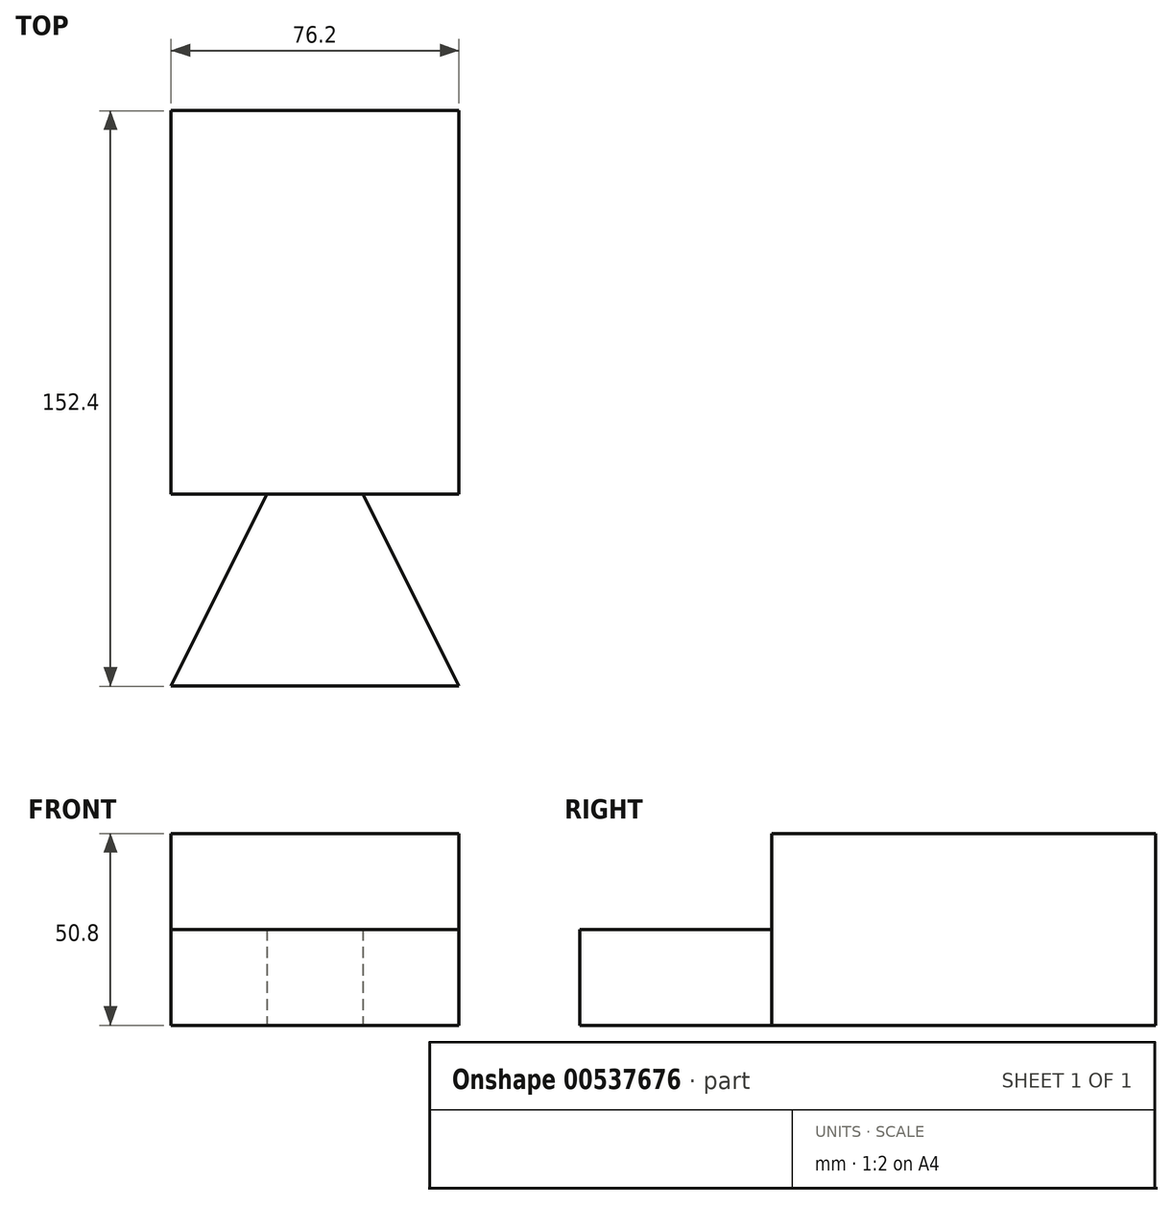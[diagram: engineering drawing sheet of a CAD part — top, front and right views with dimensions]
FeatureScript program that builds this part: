
annotation { "Feature Type Name" : "Feature", "Feature Type Description" : "" }
export const myFeature = defineFeature(function(context is Context, id is Id, definition is map)
    precondition{}
    {
        {
            var Q0;
            Q0=qCreatedBy(makeId("Top.planeOp"),FACE);
            var sketch = newSketch(context, id + "F0", { "sketchPlane" : qUnion([Q0])});
            skLineSegment(sketch, "E0.bottom", {"start": v(-123.66, 76.55) * mm, "end": v(-47.46, 76.55) * mm});
            skLineSegment(sketch, "E0.top", {"start": v(-123.66, -25.05) * mm, "end": v(-47.46, -25.05) * mm});
            skLineSegment(sketch, "E0.left", {"start": v(-123.66, 76.55) * mm, "end": v(-123.66, -25.05) * mm});
            skLineSegment(sketch, "E0.right", {"start": v(-47.46, 76.55) * mm, "end": v(-47.46, -25.05) * mm});
            skLineSegment(sketch, "E1", {"start": v(-123.66, -25.05) * mm, "end": v(-98.26, -25.05) * mm});
            skLineSegment(sketch, "E2", {"start": v(-72.86, -25.05) * mm, "end": v(-47.46, -25.05) * mm});
            skLineSegment(sketch, "E3", {"start": v(-123.66, -75.85) * mm, "end": v(-47.46, -75.85) * mm});
            skLineSegment(sketch, "E4", {"start": v(-98.26, -25.05) * mm, "end": v(-123.66, -75.85) * mm});
            skLineSegment(sketch, "E5", {"start": v(-72.86, -25.05) * mm, "end": v(-47.46, -75.85) * mm});
            skSolve(sketch);
        }
        {
            var Q0;
            Q0=makeQuery(id+"F0.imprint","IMPRINT",FACE,{"disambiguationData":[TD([[makeQuery(id+"F0.imprint","IMPRINT",EDGE,{"derivedFrom":sQuery(id+"F0.wireOp",EDGE,"E0.bottom")}),-1.0]])]});
            extrude(context, id + "F1", {"entities" : qUnion([Q0]), "depth" : 50.8 * mm, "offsetDistance" : 25.4 * mm});
        }
        {
            var Q0;
            Q0=makeQuery(id+"F0.imprint","IMPRINT",FACE,{"disambiguationData":[TD([[makeQuery(id+"F0.imprint","IMPRINT",EDGE,{"derivedFrom":sQuery(id+"F0.wireOp",EDGE,"E0.top")}),-1.0]])]});
            extrude(context, id + "F2", {"entities" : qUnion([Q0]), "operationType" : NewBodyOperationType.ADD, "depth" : 25.4 * mm, "offsetDistance" : 25.4 * mm});
        }
    });
